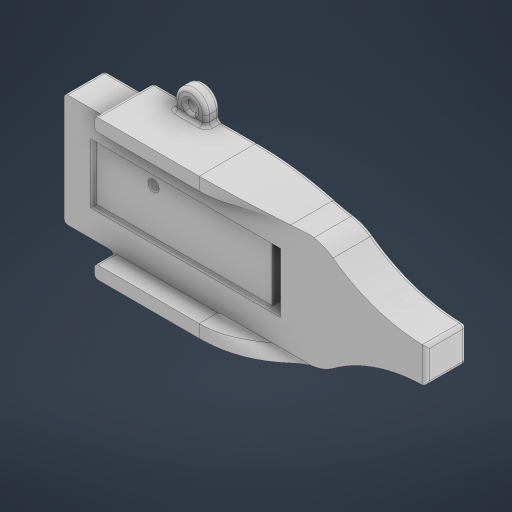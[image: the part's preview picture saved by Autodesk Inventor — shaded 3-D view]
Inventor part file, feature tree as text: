
AUTODESK INVENTOR PART (.ipt)
format: ipt  version: 2024.1 (Build 281209000, 209)  size: 4,624,896 bytes
history: native  units: mm
features: sketch x8, extrude x7, other x4, fillet x3, projected_geometry x3, loft x1, plane x1, mirror x1, hole x1
ambient origin geometry x8: Origin, YZ Plane, XZ Plane, XY Plane, X Axis, Y Axis, Z Axis, Center Point
bodies: Solid1 (feature_tree)
feature tree (29):
  other  "3D_PCB1_2024-08-12"
  extrude  "Extrusion1"  Depth=1.0mm
  extrude  "Extrusion2"  Depth=10.0mm TaperAngle=0.0deg
  extrude  "Extrusion3"  Depth=10.0mm
  extrude  "Extrusion4"  Depth=20.0mm
  extrude  "Extrusion5"  Depth=0.3mm
  extrude  "Extrusion6"  Depth=4.0mm
  extrude  "Extrusion7"  Depth=9.0mm
  loft  "Loft1"
  plane  "Work Plane1"
  mirror  "Mirror1"
  hole  "Hole1"  [1 undecoded]
  fillet  "Fillet1"  Radius=10.0mm
  fillet  "Fillet3"  Radius=50.0mm
  fillet  "Fillet4"  Radius=50.0mm
  sketch  "Sketch1"  dims[d0=1.0mm d1=32.28mm]
  sketch  "Sketch2"  dims[d2=1.6mm d3=0.0mm d4=10.0mm d5=0.0mm]
  projected_geometry  "Projected Loop1"
  sketch  "Sketch3"  dims[d6=4.0mm d7=10.0mm]
  projected_geometry  "Projected Loop2"
  sketch  "Sketch4"  dims[d8=4.0mm d9=20.0mm]
  sketch  "Sketch5"  dims[d10=16.9mm d11=0.0mm d12=0.3mm]
  sketch  "Sketch6"  dims[d13=10.6mm d14=0.0mm d15=4.0mm]
  sketch  "Sketch7"  dims[d16=2.5mm d17=0.0mm d18=9.0mm]
  projected_geometry  "Projected Loop3"
  sketch  "Sketch8"  dims[d19=27.5mm d20=4.0mm d21=0.0mm d22=3.0mm d23=6.0mm d24=6.3mm d25=2.0mm d26=90.0deg d27=8.0mm d28=20.594885mm d32=34.061mm d33=10.0mm d36=50.0mm d37=50.0mm d38=10.0mm d39=0.0mm d40=1.0mm d41=0.0mm d42=90.0deg d43=10.0mm d44=90.0deg d45=50.0mm d46=1.0mm d29=1.0mm d30=0.0mm d31=0.0mm]
  other  "Edges1"
  other  "Edges2"
  other  "3D_PCB1_2024-08-12.obj"
note: 1 required parameter value undecoded (feature->parameter linkage not recoverable at this tier; creation-order binding heuristic only, values carry confidence <= 0.55)
